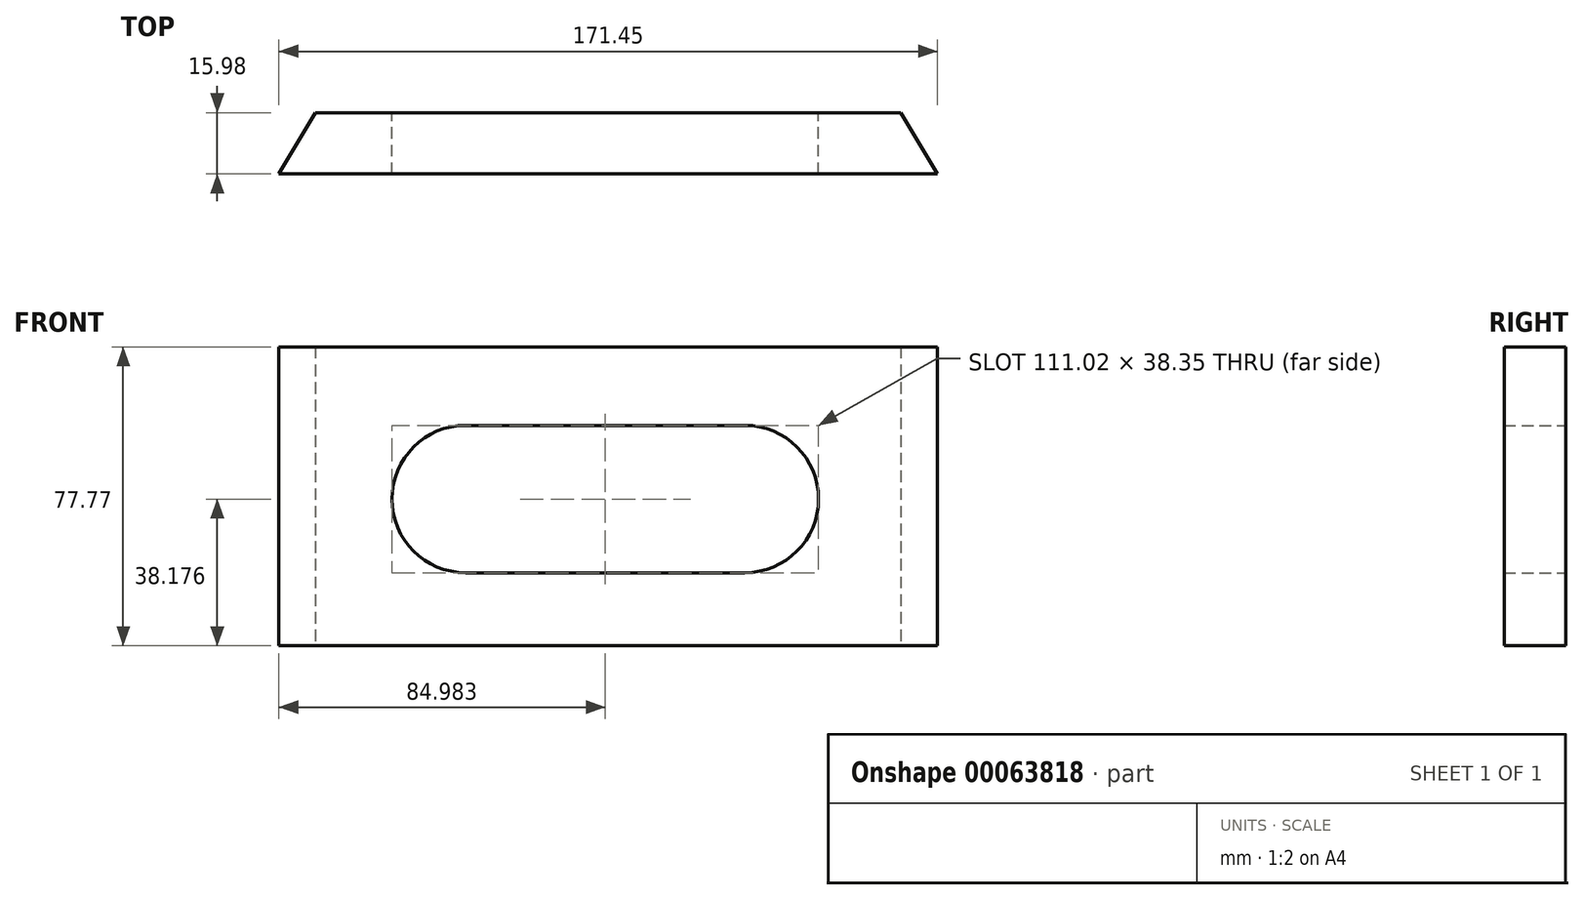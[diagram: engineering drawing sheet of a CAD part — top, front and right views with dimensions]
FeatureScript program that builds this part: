
annotation { "Feature Type Name" : "Feature", "Feature Type Description" : "" }
export const myFeature = defineFeature(function(context is Context, id is Id, definition is map)
    precondition{}
    {
        {
            var Q0;
            Q0=qCreatedBy(makeId("Top.planeOp"),FACE);
            var sketch = newSketch(context, id + "F0", { "sketchPlane" : qUnion([Q0])});
            skLineSegment(sketch, "E0", {"start": v(-78.8, 39.96) * mm, "end": v(73.6, 39.96) * mm});
            skLineSegment(sketch, "E1", {"start": v(73.6, 39.96) * mm, "end": v(83.12, 23.98) * mm});
            skLineSegment(sketch, "E2", {"start": v(83.12, 23.98) * mm, "end": v(-88.33, 23.98) * mm});
            skLineSegment(sketch, "E3", {"start": v(-88.33, 23.98) * mm, "end": v(-78.8, 39.96) * mm});
            skSolve(sketch);
        }
        {
            var Q0;
            Q0=makeQuery(id+"F0.imprint","IMPRINT",FACE,{"disambiguationData":[TD([[makeQuery(id+"F0.imprint","IMPRINT",EDGE,{"derivedFrom":sQuery(id+"F0.wireOp",EDGE,"E0")}),-1.0]])]});
            extrude(context, id + "F1", {"entities" : qUnion([Q0]), "depth" : 77.77 * mm});
        }
        {
            var Q0;
            Q0=makeQuery(id+"F1.opExtrude","SWEPT_FACE",FACE,{"disambiguationData":[OSD([sQuery(id+"F0.wireOp",EDGE,"E0")])]});
            var sketch = newSketch(context, id + "F2", { "sketchPlane" : qUnion([Q0])});
            skLineSegment(sketch, "E4", {"start": v(-32.99, 57.35) * mm, "end": v(39.68, 57.35) * mm});
            skLineSegment(sketch, "E5", {"start": v(39.68, 19) * mm, "end": v(-32.99, 19) * mm});
            skArc(sketch, "E6", {"start": v(39.68, 19) * mm, "mid": v(58.86, 38.18) * mm, "end": v(39.68, 57.35) * mm});
            skArc(sketch, "E7", {"start": v(-32.99, 57.35) * mm, "mid": v(-52.17, 38.18) * mm, "end": v(-32.99, 19) * mm});
            skSolve(sketch);
        }
        {
            var Q0;
            Q0=makeQuery(id+"F2.imprint","IMPRINT",FACE,{"disambiguationData":[TD([[makeQuery(id+"F2.imprint","IMPRINT",EDGE,{"derivedFrom":sQuery(id+"F2.wireOp",EDGE,"E4")}),-1.0]])]});
            extrude(context, id + "F3", {"entities" : qUnion([Q0]), "operationType" : NewBodyOperationType.REMOVE, "oppositeDirection" : true, "depth" : 25.4 * mm});
        }
    });
